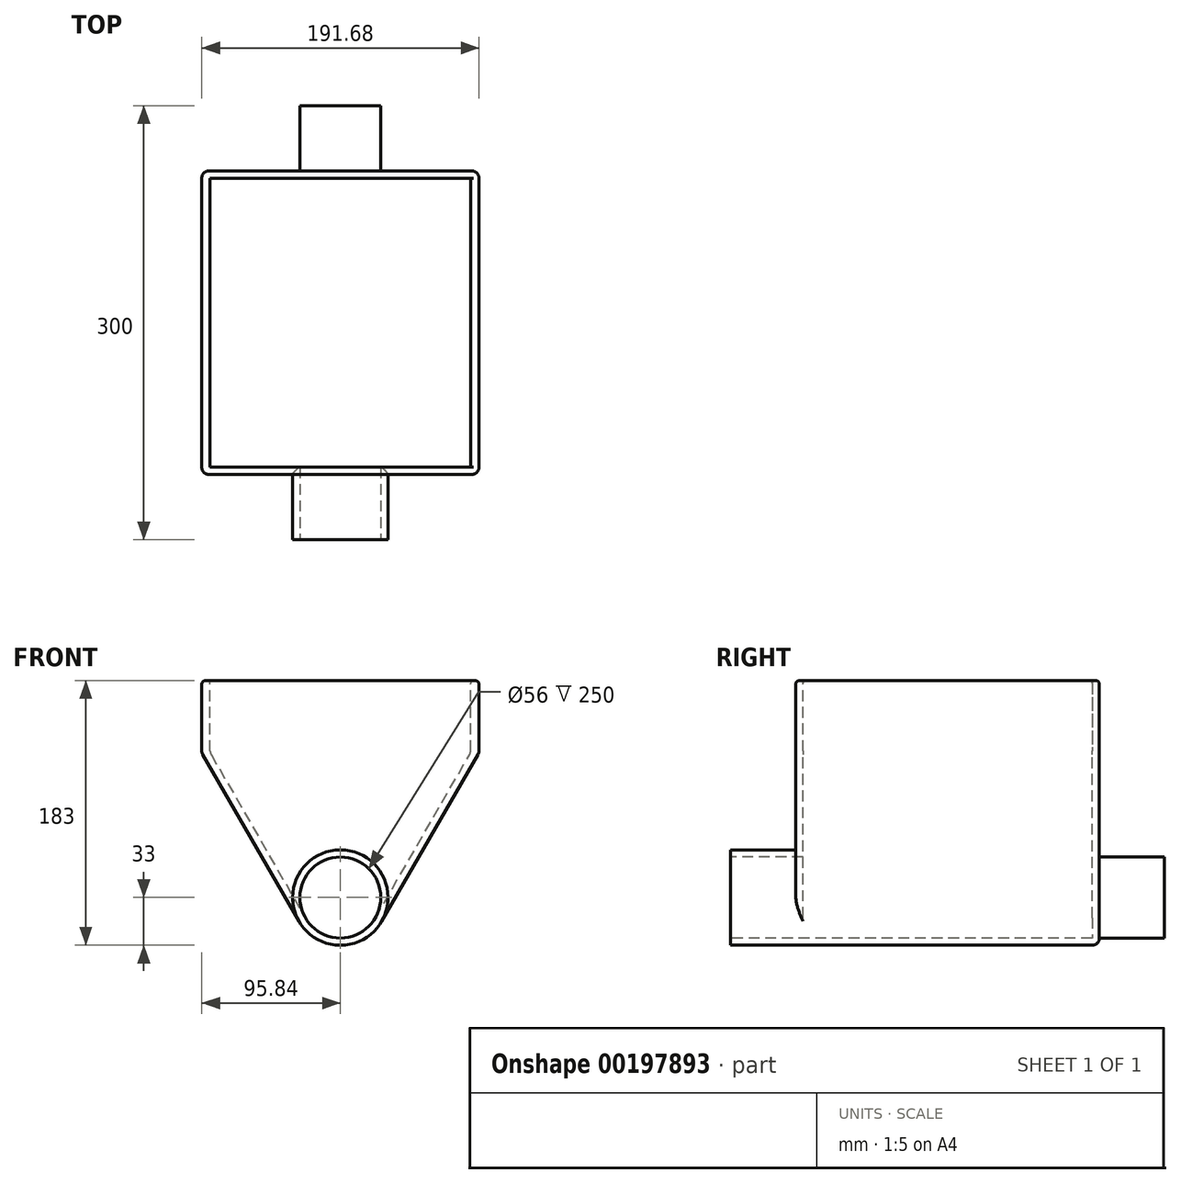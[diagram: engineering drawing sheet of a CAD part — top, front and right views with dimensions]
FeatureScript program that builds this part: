
annotation { "Feature Type Name" : "Feature", "Feature Type Description" : "" }
export const myFeature = defineFeature(function(context is Context, id is Id, definition is map)
    precondition{}
    {
        {
            var Q0;
            Q0=qCreatedBy(makeId("Front.planeOp"),FACE);
            var sketch = newSketch(context, id + "F0", { "sketchPlane" : qUnion([Q0])});
            skArc(sketch, "E0", {"start": v(-24.25, -14) * mm, "mid": v(0, -28) * mm, "end": v(24.25, -14) * mm});
            skArc(sketch, "E1", {"start": v(-28.58, -16.5) * mm, "mid": v(0, -33) * mm, "end": v(28.58, -16.5) * mm});
            skLineSegment(sketch, "E2", {"start": v(-28.58, -16.5) * mm, "end": v(-95.84, 100) * mm});
            skLineSegment(sketch, "E3", {"start": v(-95.84, 100) * mm, "end": v(-90.07, 100) * mm});
            skLineSegment(sketch, "E4", {"start": v(-90.07, 100) * mm, "end": v(-24.25, -14) * mm});
            skLineSegment(sketch, "E5", {"start": v(24.25, -14) * mm, "end": v(90.07, 100) * mm});
            skLineSegment(sketch, "E6", {"start": v(90.07, 100) * mm, "end": v(95.84, 100) * mm});
            skLineSegment(sketch, "E7", {"start": v(95.84, 100) * mm, "end": v(28.58, -16.5) * mm});
            skLineSegment(sketch, "E8", {"start": v(-95.84, 100) * mm, "end": v(-95.84, 150) * mm});
            skLineSegment(sketch, "E9", {"start": v(-95.84, 150) * mm, "end": v(-90.07, 150) * mm});
            skLineSegment(sketch, "E10", {"start": v(-90.07, 150) * mm, "end": v(-90.07, 100) * mm});
            skLineSegment(sketch, "E11", {"start": v(95.84, 100) * mm, "end": v(95.84, 150) * mm});
            skLineSegment(sketch, "E12", {"start": v(95.84, 150) * mm, "end": v(90.07, 150) * mm});
            skLineSegment(sketch, "E13", {"start": v(90.07, 150) * mm, "end": v(90.07, 100) * mm});
            skSolve(sketch);
        }
        {
            var Q0;
            Q0 = qSketchRegion(id + "F0", true);
            extrude(context, id + "F1", {"entities" : qUnion([Q0]), "oppositeDirection" : true, "depth" : 200 * mm});
        }
        {
            var Q0;
            Q0=makeQuery(id+"F1.opExtrude","CAP_FACE",FACE,{"disambiguationData":[OSD([sQuery(id+"F0.wireOp",EDGE,"E0"),sQuery(id+"F0.wireOp",EDGE,"E1"),sQuery(id+"F0.wireOp",EDGE,"E2"),sQuery(id+"F0.wireOp",EDGE,"E4"),sQuery(id+"F0.wireOp",EDGE,"E5"),sQuery(id+"F0.wireOp",EDGE,"E7"),sQuery(id+"F0.wireOp",EDGE,"E8"),sQuery(id+"F0.wireOp",EDGE,"E9"),sQuery(id+"F0.wireOp",EDGE,"E10"),sQuery(id+"F0.wireOp",EDGE,"E11"),sQuery(id+"F0.wireOp",EDGE,"E12"),sQuery(id+"F0.wireOp",EDGE,"E13")])],"isStart":true});
            var sketch = newSketch(context, id + "F2", { "sketchPlane" : qUnion([Q0])});
            skCircle(sketch, "E14", {"center": v(0, 0) * mm, "radius": 33 * mm});
            skCircle(sketch, "E15", {"center": v(0, 0) * mm, "radius": 28 * mm});
            skSolve(sketch);
        }
        {
            var Q0;
            {var subQ0=sQuery(id+"F2.wireOp",EDGE,"E14");var subQ1=makeQuery(id+"F1.opExtrude","CAP_EDGE",EDGE,{"disambiguationData":[OSD([sQuery(id+"F0.wireOp",EDGE,"E4")])],"isStart":true});var subQ2=makeQuery(id+"F2.imprint","INTERSECT",VERTEX,{"derivedFrom":[subQ1,subQ0]});Q0=makeQuery(id+"F2.imprint","IMPRINT",FACE,{"disambiguationData":[TD([[makeQuery(id+"F2.imprint","IMPRINT",EDGE,{"disambiguationData":[TD([[subQ2,1.0]])],"derivedFrom":subQ0}),1.0]])]});}
            var Q1;
            {var subQ5=sQuery(id+"F2.wireOp",EDGE,"E14");var subQ8=makeQuery(id+"F2.imprint","INTERSECT",VERTEX,{"derivedFrom":[makeQuery(id+"F1.opExtrude","CAP_EDGE",EDGE,{"disambiguationData":[OSD([sQuery(id+"F0.wireOp",EDGE,"E2")])],"isStart":true}),subQ5]});Q1=makeQuery(id+"F2.imprint","IMPRINT",FACE,{"disambiguationData":[TD([[makeQuery(id+"F2.imprint","IMPRINT",EDGE,{"disambiguationData":[TD([[subQ8,-1.0]])],"derivedFrom":subQ5}),1.0]])]});}
            extrude(context, id + "F3", {"entities" : qUnion([Q0, Q1]), "operationType" : NewBodyOperationType.ADD, "depth" : 50 * mm});
        }
        {
            var Q0;
            Q0=makeQuery(id+"F1.opExtrude","CAP_FACE",FACE,{"disambiguationData":[OSD([sQuery(id+"F0.wireOp",EDGE,"E0"),sQuery(id+"F0.wireOp",EDGE,"E1"),sQuery(id+"F0.wireOp",EDGE,"E2"),sQuery(id+"F0.wireOp",EDGE,"E4"),sQuery(id+"F0.wireOp",EDGE,"E5"),sQuery(id+"F0.wireOp",EDGE,"E7"),sQuery(id+"F0.wireOp",EDGE,"E8"),sQuery(id+"F0.wireOp",EDGE,"E9"),sQuery(id+"F0.wireOp",EDGE,"E10"),sQuery(id+"F0.wireOp",EDGE,"E11"),sQuery(id+"F0.wireOp",EDGE,"E12"),sQuery(id+"F0.wireOp",EDGE,"E13")])],"isStart":false});
            var sketch = newSketch(context, id + "F4", { "sketchPlane" : qUnion([Q0])});
            skCircle(sketch, "E16", {"center": v(0, 0) * mm, "radius": 28 * mm});
            skCircle(sketch, "E17", {"center": v(0, 0) * mm, "radius": 33 * mm});
            skSolve(sketch);
        }
        {
            var Q0;
            {var subQ0=sQuery(id+"F4.wireOp",EDGE,"E16");Q0=makeQuery(id+"F4.imprint","IMPRINT",FACE,{"disambiguationData":[TD([[makeQuery(id+"F4.imprint","IMPRINT",EDGE,{"disambiguationData":[OD(1.0)],"derivedFrom":subQ0}),-1.0]])]});}
            var Q1;
            {var subQ7=sQuery(id+"F4.wireOp",EDGE,"E16");Q1=makeQuery(id+"F4.imprint","IMPRINT",FACE,{"disambiguationData":[TD([[makeQuery(id+"F4.imprint","IMPRINT",EDGE,{"disambiguationData":[OD(0.0)],"derivedFrom":subQ7}),1.0]])]});}
            extrude(context, id + "F5", {"entities" : qUnion([Q0, Q1]), "operationType" : NewBodyOperationType.ADD, "depth" : 50 * mm});
        }
        {
            var Q0;
            {var subQ0=sQuery(id+"F0.wireOp",EDGE,"E11");var subQ1=sQuery(id+"F0.wireOp",EDGE,"E7");var subQ2=sQuery(id+"F0.wireOp",EDGE,"E5");var subQ3=sQuery(id+"F0.wireOp",EDGE,"E1");var subQ4=sQuery(id+"F0.wireOp",EDGE,"E12");var subQ6=sQuery(id+"F0.wireOp",EDGE,"E13");Q0=makeQuery(id+"F3.boolean.opBoolean","SPLIT",FACE,{"disambiguationData":[TD([makeQuery(id+"F1.opExtrude","SWEPT_FACE",FACE,{"disambiguationData":[OSD([subQ2])]})])],"derivedFrom":makeQuery(id+"F1.opExtrude","CAP_FACE",FACE,{"disambiguationData":[OSD([sQuery(id+"F0.wireOp",EDGE,"E0"),subQ3,sQuery(id+"F0.wireOp",EDGE,"E2"),sQuery(id+"F0.wireOp",EDGE,"E4"),subQ2,subQ1,sQuery(id+"F0.wireOp",EDGE,"E8"),sQuery(id+"F0.wireOp",EDGE,"E9"),sQuery(id+"F0.wireOp",EDGE,"E10"),subQ0,subQ4,subQ6])],"isStart":true})});}
            var Q1;
            {var subQ0=sQuery(id+"F0.wireOp",EDGE,"E4");var subQ2=sQuery(id+"F0.wireOp",EDGE,"E2");var subQ3=sQuery(id+"F0.wireOp",EDGE,"E8");var subQ4=sQuery(id+"F0.wireOp",EDGE,"E1");var subQ5=sQuery(id+"F0.wireOp",EDGE,"E10");var subQ6=sQuery(id+"F0.wireOp",EDGE,"E9");Q1=makeQuery(id+"F3.boolean.opBoolean","SPLIT",FACE,{"disambiguationData":[TD([makeQuery(id+"F1.opExtrude","SWEPT_FACE",FACE,{"disambiguationData":[OSD([subQ2])]})])],"derivedFrom":makeQuery(id+"F1.opExtrude","CAP_FACE",FACE,{"disambiguationData":[OSD([sQuery(id+"F0.wireOp",EDGE,"E0"),subQ4,subQ2,subQ0,sQuery(id+"F0.wireOp",EDGE,"E5"),sQuery(id+"F0.wireOp",EDGE,"E7"),subQ3,subQ6,subQ5,sQuery(id+"F0.wireOp",EDGE,"E11"),sQuery(id+"F0.wireOp",EDGE,"E12"),sQuery(id+"F0.wireOp",EDGE,"E13")])],"isStart":true})});}
            extrude(context, id + "F6", {"entities" : qUnion([Q0, Q1]), "operationType" : NewBodyOperationType.ADD, "depth" : 5 * mm});
        }
        {
            var Q0;
            Q0=qCreatedBy(makeId("Right.planeOp"),FACE);
            var sketch = newSketch(context, id + "F7", { "sketchPlane" : qUnion([Q0])});
            skLineSegment(sketch, "E18.bottom", {"start": v(-5, 110) * mm, "end": v(0, 110) * mm});
            skLineSegment(sketch, "E18.top", {"start": v(-5, 150) * mm, "end": v(0, 150) * mm});
            skLineSegment(sketch, "E18.left", {"start": v(-5, 110) * mm, "end": v(-5, 150) * mm});
            skLineSegment(sketch, "E18.right", {"start": v(0, 110) * mm, "end": v(0, 150) * mm});
            skSolve(sketch);
        }
        {
            var Q0;
            Q0=makeQuery(id+"F7.imprint","IMPRINT",FACE,{"disambiguationData":[TD([[makeQuery(id+"F7.imprint","IMPRINT",EDGE,{"derivedFrom":sQuery(id+"F7.wireOp",EDGE,"E18.bottom")}),1.0]])]});
            var Q1;
            {var subQ0=sQuery(id+"F0.wireOp",EDGE,"E10");Q1=makeQuery(id+"F6.boolean.opBoolean","MERGE",FACE,{"derivedFrom":[makeQuery(id+"F1.opExtrude","SWEPT_FACE",FACE,{"disambiguationData":[OSD([subQ0])]}),makeQuery(id+"F6.opExtrude","SWEPT_FACE",FACE,{"disambiguationData":[OSD([subQ0])]})]});}
            var Q2;
            {var subQ0=sQuery(id+"F0.wireOp",EDGE,"E13");Q2=makeQuery(id+"F6.boolean.opBoolean","MERGE",FACE,{"derivedFrom":[makeQuery(id+"F1.opExtrude","SWEPT_FACE",FACE,{"disambiguationData":[OSD([subQ0])]}),makeQuery(id+"F6.opExtrude","SWEPT_FACE",FACE,{"disambiguationData":[OSD([subQ0])]})]});}
            extrude(context, id + "F8", {"entities" : qUnion([Q0]), "endBound" : BoundingType.UP_TO_SURFACE, "oppositeDirection" : true, "endBoundEntityFace" : qUnion([Q1]), "depth" : 25 * mm, "hasSecondDirection" : true, "secondDirectionBound" : SecondDirectionBoundingType.UP_TO_SURFACE, "secondDirectionOppositeDirection" : false, "secondDirectionBoundEntityFace" : qUnion([Q2]), "secondDirectionDepth" : 25 * mm});
        }
        {
            var Q0;
            Q0=makeQuery(id+"F8.opExtrude","SWEPT_FACE",FACE,{"disambiguationData":[OSD([sQuery(id+"F7.wireOp",EDGE,"E18.bottom")])]});
            var Q1;
            Q1=makeQuery(id+"F1.opExtrude","SWEPT_BODY",BODY,{"disambiguationData":[OSD([sQuery(id+"F0.wireOp",EDGE,"E0"),sQuery(id+"F0.wireOp",EDGE,"E1"),sQuery(id+"F0.wireOp",EDGE,"E2"),sQuery(id+"F0.wireOp",EDGE,"E4"),sQuery(id+"F0.wireOp",EDGE,"E5"),sQuery(id+"F0.wireOp",EDGE,"E7"),sQuery(id+"F0.wireOp",EDGE,"E8"),sQuery(id+"F0.wireOp",EDGE,"E9"),sQuery(id+"F0.wireOp",EDGE,"E10"),sQuery(id+"F0.wireOp",EDGE,"E11"),sQuery(id+"F0.wireOp",EDGE,"E12"),sQuery(id+"F0.wireOp",EDGE,"E13")])]});
            extrude(context, id + "F9", {"entities" : qUnion([Q0]), "operationType" : NewBodyOperationType.ADD, "endBound" : BoundingType.UP_TO_BODY, "endBoundEntityBody" : qUnion([Q1]), "depth" : 25 * mm});
        }
        {
            var Q0;
            {var subQ0=sQuery(id+"F0.wireOp",EDGE,"E11");var subQ1=sQuery(id+"F0.wireOp",EDGE,"E7");var subQ2=sQuery(id+"F0.wireOp",EDGE,"E5");var subQ3=sQuery(id+"F0.wireOp",EDGE,"E1");var subQ4=sQuery(id+"F0.wireOp",EDGE,"E12");var subQ5=sQuery(id+"F0.wireOp",EDGE,"E13");Q0=makeQuery(id+"F5.boolean.opBoolean","SPLIT",FACE,{"disambiguationData":[TD([makeQuery(id+"F1.opExtrude","SWEPT_FACE",FACE,{"disambiguationData":[OSD([subQ2])]})])],"derivedFrom":makeQuery(id+"F1.opExtrude","CAP_FACE",FACE,{"disambiguationData":[OSD([sQuery(id+"F0.wireOp",EDGE,"E0"),subQ3,sQuery(id+"F0.wireOp",EDGE,"E2"),sQuery(id+"F0.wireOp",EDGE,"E4"),subQ2,subQ1,sQuery(id+"F0.wireOp",EDGE,"E8"),sQuery(id+"F0.wireOp",EDGE,"E9"),sQuery(id+"F0.wireOp",EDGE,"E10"),subQ0,subQ4,subQ5])],"isStart":false})});}
            var Q1;
            {var subQ0=sQuery(id+"F0.wireOp",EDGE,"E4");var subQ1=sQuery(id+"F0.wireOp",EDGE,"E2");var subQ2=sQuery(id+"F0.wireOp",EDGE,"E8");var subQ3=sQuery(id+"F0.wireOp",EDGE,"E1");var subQ4=sQuery(id+"F0.wireOp",EDGE,"E10");var subQ5=sQuery(id+"F0.wireOp",EDGE,"E9");Q1=makeQuery(id+"F5.boolean.opBoolean","SPLIT",FACE,{"disambiguationData":[TD([makeQuery(id+"F1.opExtrude","SWEPT_FACE",FACE,{"disambiguationData":[OSD([subQ1])]})])],"derivedFrom":makeQuery(id+"F1.opExtrude","CAP_FACE",FACE,{"disambiguationData":[OSD([sQuery(id+"F0.wireOp",EDGE,"E0"),subQ3,subQ1,subQ0,sQuery(id+"F0.wireOp",EDGE,"E5"),sQuery(id+"F0.wireOp",EDGE,"E7"),subQ2,subQ5,subQ4,sQuery(id+"F0.wireOp",EDGE,"E11"),sQuery(id+"F0.wireOp",EDGE,"E12"),sQuery(id+"F0.wireOp",EDGE,"E13")])],"isStart":false})});}
            extrude(context, id + "F10", {"entities" : qUnion([Q0, Q1]), "operationType" : NewBodyOperationType.ADD, "depth" : 5 * mm});
        }
        {
            var Q0;
            Q0=qCreatedBy(makeId("Right.planeOp"),FACE);
            var sketch = newSketch(context, id + "F11", { "sketchPlane" : qUnion([Q0])});
            skLineSegment(sketch, "E19.bottom", {"start": v(205, 150) * mm, "end": v(200, 150) * mm});
            skLineSegment(sketch, "E19.top", {"start": v(205, 110) * mm, "end": v(200, 110) * mm});
            skLineSegment(sketch, "E19.left", {"start": v(205, 150) * mm, "end": v(205, 110) * mm});
            skLineSegment(sketch, "E19.right", {"start": v(200, 150) * mm, "end": v(200, 110) * mm});
            skSolve(sketch);
        }
        {
            var Q0;
            Q0 = qSketchRegion(id + "F11", true);
            var Q1;
            {var subQ0=sQuery(id+"F0.wireOp",EDGE,"E10");Q1=makeQuery(id+"F10.boolean.opBoolean","MERGE",FACE,{"derivedFrom":[makeQuery(id+"F6.boolean.opBoolean","MERGE",FACE,{"derivedFrom":[makeQuery(id+"F1.opExtrude","SWEPT_FACE",FACE,{"disambiguationData":[OSD([subQ0])]}),makeQuery(id+"F6.opExtrude","SWEPT_FACE",FACE,{"disambiguationData":[OSD([subQ0])]})]}),makeQuery(id+"F10.opExtrude","SWEPT_FACE",FACE,{"disambiguationData":[OSD([subQ0])]})]});}
            var Q2;
            {var subQ0=sQuery(id+"F0.wireOp",EDGE,"E13");Q2=makeQuery(id+"F10.boolean.opBoolean","MERGE",FACE,{"derivedFrom":[makeQuery(id+"F6.boolean.opBoolean","MERGE",FACE,{"derivedFrom":[makeQuery(id+"F1.opExtrude","SWEPT_FACE",FACE,{"disambiguationData":[OSD([subQ0])]}),makeQuery(id+"F6.opExtrude","SWEPT_FACE",FACE,{"disambiguationData":[OSD([subQ0])]})]}),makeQuery(id+"F10.opExtrude","SWEPT_FACE",FACE,{"disambiguationData":[OSD([subQ0])]})]});}
            extrude(context, id + "F12", {"entities" : qUnion([Q0]), "endBound" : BoundingType.UP_TO_SURFACE, "oppositeDirection" : true, "endBoundEntityFace" : qUnion([Q1]), "depth" : 25 * mm, "hasSecondDirection" : true, "secondDirectionBound" : SecondDirectionBoundingType.UP_TO_SURFACE, "secondDirectionOppositeDirection" : false, "secondDirectionBoundEntityFace" : qUnion([Q2]), "secondDirectionDepth" : 25 * mm});
        }
        {
            var Q0;
            Q0=makeQuery(id+"F12.opExtrude","SWEPT_FACE",FACE,{"disambiguationData":[OSD([sQuery(id+"F11.wireOp",EDGE,"E19.top")])]});
            var Q1;
            Q1=makeQuery(id+"F1.opExtrude","SWEPT_BODY",BODY,{"disambiguationData":[OSD([sQuery(id+"F0.wireOp",EDGE,"E0"),sQuery(id+"F0.wireOp",EDGE,"E1"),sQuery(id+"F0.wireOp",EDGE,"E2"),sQuery(id+"F0.wireOp",EDGE,"E4"),sQuery(id+"F0.wireOp",EDGE,"E5"),sQuery(id+"F0.wireOp",EDGE,"E7"),sQuery(id+"F0.wireOp",EDGE,"E8"),sQuery(id+"F0.wireOp",EDGE,"E9"),sQuery(id+"F0.wireOp",EDGE,"E10"),sQuery(id+"F0.wireOp",EDGE,"E11"),sQuery(id+"F0.wireOp",EDGE,"E12"),sQuery(id+"F0.wireOp",EDGE,"E13")])]});
            extrude(context, id + "F13", {"entities" : qUnion([Q0]), "operationType" : NewBodyOperationType.ADD, "endBound" : BoundingType.UP_TO_BODY, "endBoundEntityBody" : qUnion([Q1]), "depth" : 25 * mm});
        }
        {
            var Q0;
            {var subQ0=sQuery(id+"F0.wireOp",EDGE,"E5");var subQ1=makeQuery(id+"F1.opExtrude","SWEPT_FACE",FACE,{"disambiguationData":[OSD([subQ0])]});var subQ3=sQuery(id+"F0.wireOp",EDGE,"E0");Q0=makeQuery(id+"F9.boolean.opBoolean","MERGE",EDGE,{"derivedFrom":[makeQuery(id+"F3.boolean.opBoolean","SPLIT",EDGE,{"disambiguationData":[TD([makeQuery(id+"F1.opExtrude","SWEPT_FACE",FACE,{"disambiguationData":[OSD([subQ3])]})])],"derivedFrom":makeQuery(id+"F1.opExtrude","CAP_EDGE",EDGE,{"disambiguationData":[OSD([subQ0])],"isStart":true})}),makeQuery(id+"F9.opExtrude","TWEAK_EDGE",EDGE,{"derivedFrom":[makeQuery(id+"F6.boolean.opBoolean","MERGE",FACE,{"derivedFrom":[subQ1,makeQuery(id+"F6.opExtrude","SWEPT_FACE",FACE,{"disambiguationData":[OSD([subQ0])]})]}),makeQuery(id+"F8.opExtrude","TWEAK_EDGE",EDGE,{"derivedFrom":[makeQuery(id+"F7.imprint","IMPRINT",EDGE,{"derivedFrom":sQuery(id+"F7.wireOp",EDGE,"E18.bottom")}),makeQuery(id+"F7.imprint","IMPRINT",EDGE,{"derivedFrom":sQuery(id+"F7.wireOp",EDGE,"E18.right")})]})]})]});}
            var Q1;
            {var subQ0=sQuery(id+"F7.wireOp",EDGE,"E18.right");var subQ1=sQuery(id+"F0.wireOp",EDGE,"E13");Q1=makeQuery(id+"F9.boolean.opBoolean","MERGE",EDGE,{"derivedFrom":[makeQuery(id+"F8.opExtrude","TWEAK_EDGE",EDGE,{"derivedFrom":[makeQuery(id+"F6.boolean.opBoolean","MERGE",FACE,{"derivedFrom":[makeQuery(id+"F1.opExtrude","SWEPT_FACE",FACE,{"disambiguationData":[OSD([subQ1])]}),makeQuery(id+"F6.opExtrude","SWEPT_FACE",FACE,{"disambiguationData":[OSD([subQ1])]})]}),makeQuery(id+"F7.imprint","IMPRINT",EDGE,{"derivedFrom":subQ0})]}),makeQuery(id+"F9.opExtrude","SWEPT_EDGE",EDGE,{"disambiguationData":[OSD([subQ1,sQuery(id+"F7.wireOp",EDGE,"E18.bottom"),subQ0])]})]});}
            var Q2;
            {var subQ0=sQuery(id+"F0.wireOp",EDGE,"E4");var subQ1=makeQuery(id+"F1.opExtrude","SWEPT_FACE",FACE,{"disambiguationData":[OSD([subQ0])]});var subQ4=sQuery(id+"F0.wireOp",EDGE,"E0");Q2=makeQuery(id+"F9.boolean.opBoolean","MERGE",EDGE,{"derivedFrom":[makeQuery(id+"F3.boolean.opBoolean","SPLIT",EDGE,{"disambiguationData":[TD([makeQuery(id+"F1.opExtrude","SWEPT_FACE",FACE,{"disambiguationData":[OSD([subQ4])]})])],"derivedFrom":makeQuery(id+"F1.opExtrude","CAP_EDGE",EDGE,{"disambiguationData":[OSD([subQ0])],"isStart":true})}),makeQuery(id+"F9.opExtrude","TWEAK_EDGE",EDGE,{"derivedFrom":[makeQuery(id+"F6.boolean.opBoolean","MERGE",FACE,{"derivedFrom":[subQ1,makeQuery(id+"F6.opExtrude","SWEPT_FACE",FACE,{"disambiguationData":[OSD([subQ0])]})]}),makeQuery(id+"F8.opExtrude","TWEAK_EDGE",EDGE,{"derivedFrom":[makeQuery(id+"F7.imprint","IMPRINT",EDGE,{"derivedFrom":sQuery(id+"F7.wireOp",EDGE,"E18.bottom")}),makeQuery(id+"F7.imprint","IMPRINT",EDGE,{"derivedFrom":sQuery(id+"F7.wireOp",EDGE,"E18.right")})]})]})]});}
            var Q3;
            {var subQ0=sQuery(id+"F7.wireOp",EDGE,"E18.right");var subQ1=sQuery(id+"F0.wireOp",EDGE,"E10");Q3=makeQuery(id+"F9.boolean.opBoolean","MERGE",EDGE,{"derivedFrom":[makeQuery(id+"F8.opExtrude","TWEAK_EDGE",EDGE,{"derivedFrom":[makeQuery(id+"F6.boolean.opBoolean","MERGE",FACE,{"derivedFrom":[makeQuery(id+"F1.opExtrude","SWEPT_FACE",FACE,{"disambiguationData":[OSD([subQ1])]}),makeQuery(id+"F6.opExtrude","SWEPT_FACE",FACE,{"disambiguationData":[OSD([subQ1])]})]}),makeQuery(id+"F7.imprint","IMPRINT",EDGE,{"derivedFrom":subQ0})]}),makeQuery(id+"F9.opExtrude","SWEPT_EDGE",EDGE,{"disambiguationData":[OSD([subQ1,sQuery(id+"F7.wireOp",EDGE,"E18.bottom"),subQ0])]})]});}
            var Q4;
            {var subQ0=sQuery(id+"F11.wireOp",EDGE,"E19.right");var subQ1=sQuery(id+"F0.wireOp",EDGE,"E10");Q4=makeQuery(id+"F13.boolean.opBoolean","MERGE",EDGE,{"derivedFrom":[makeQuery(id+"F12.opExtrude","TWEAK_EDGE",EDGE,{"derivedFrom":[makeQuery(id+"F10.boolean.opBoolean","MERGE",FACE,{"derivedFrom":[makeQuery(id+"F6.boolean.opBoolean","MERGE",FACE,{"derivedFrom":[makeQuery(id+"F1.opExtrude","SWEPT_FACE",FACE,{"disambiguationData":[OSD([subQ1])]}),makeQuery(id+"F6.opExtrude","SWEPT_FACE",FACE,{"disambiguationData":[OSD([subQ1])]})]}),makeQuery(id+"F10.opExtrude","SWEPT_FACE",FACE,{"disambiguationData":[OSD([subQ1])]})]}),makeQuery(id+"F11.imprint","IMPRINT",EDGE,{"derivedFrom":subQ0})]}),makeQuery(id+"F13.opExtrude","SWEPT_EDGE",EDGE,{"disambiguationData":[OSD([subQ1,sQuery(id+"F11.wireOp",EDGE,"E19.top"),subQ0])]})]});}
            var Q5;
            {var subQ0=sQuery(id+"F0.wireOp",EDGE,"E4");var subQ1=makeQuery(id+"F1.opExtrude","SWEPT_FACE",FACE,{"disambiguationData":[OSD([subQ0])]});var subQ3=sQuery(id+"F0.wireOp",EDGE,"E0");Q5=makeQuery(id+"F13.boolean.opBoolean","MERGE",EDGE,{"derivedFrom":[makeQuery(id+"F5.boolean.opBoolean","SPLIT",EDGE,{"disambiguationData":[TD([makeQuery(id+"F1.opExtrude","SWEPT_FACE",FACE,{"disambiguationData":[OSD([subQ3])]})])],"derivedFrom":makeQuery(id+"F1.opExtrude","CAP_EDGE",EDGE,{"disambiguationData":[OSD([subQ0])],"isStart":false})}),makeQuery(id+"F13.opExtrude","TWEAK_EDGE",EDGE,{"derivedFrom":[makeQuery(id+"F10.boolean.opBoolean","MERGE",FACE,{"derivedFrom":[makeQuery(id+"F6.boolean.opBoolean","MERGE",FACE,{"derivedFrom":[subQ1,makeQuery(id+"F6.opExtrude","SWEPT_FACE",FACE,{"disambiguationData":[OSD([subQ0])]})]}),makeQuery(id+"F10.opExtrude","SWEPT_FACE",FACE,{"disambiguationData":[OSD([subQ0])]})]}),makeQuery(id+"F12.opExtrude","TWEAK_EDGE",EDGE,{"derivedFrom":[makeQuery(id+"F11.imprint","IMPRINT",EDGE,{"derivedFrom":sQuery(id+"F11.wireOp",EDGE,"E19.top")}),makeQuery(id+"F11.imprint","IMPRINT",EDGE,{"derivedFrom":sQuery(id+"F11.wireOp",EDGE,"E19.right")})]})]})]});}
            var Q6;
            {var subQ0=sQuery(id+"F11.wireOp",EDGE,"E19.right");var subQ1=sQuery(id+"F0.wireOp",EDGE,"E13");Q6=makeQuery(id+"F13.boolean.opBoolean","MERGE",EDGE,{"derivedFrom":[makeQuery(id+"F12.opExtrude","TWEAK_EDGE",EDGE,{"derivedFrom":[makeQuery(id+"F10.boolean.opBoolean","MERGE",FACE,{"derivedFrom":[makeQuery(id+"F6.boolean.opBoolean","MERGE",FACE,{"derivedFrom":[makeQuery(id+"F1.opExtrude","SWEPT_FACE",FACE,{"disambiguationData":[OSD([subQ1])]}),makeQuery(id+"F6.opExtrude","SWEPT_FACE",FACE,{"disambiguationData":[OSD([subQ1])]})]}),makeQuery(id+"F10.opExtrude","SWEPT_FACE",FACE,{"disambiguationData":[OSD([subQ1])]})]}),makeQuery(id+"F11.imprint","IMPRINT",EDGE,{"derivedFrom":subQ0})]}),makeQuery(id+"F13.opExtrude","SWEPT_EDGE",EDGE,{"disambiguationData":[OSD([subQ1,sQuery(id+"F11.wireOp",EDGE,"E19.top"),subQ0])]})]});}
            var Q7;
            {var subQ0=sQuery(id+"F0.wireOp",EDGE,"E5");var subQ1=makeQuery(id+"F1.opExtrude","SWEPT_FACE",FACE,{"disambiguationData":[OSD([subQ0])]});var subQ4=sQuery(id+"F0.wireOp",EDGE,"E0");Q7=makeQuery(id+"F13.boolean.opBoolean","MERGE",EDGE,{"derivedFrom":[makeQuery(id+"F5.boolean.opBoolean","SPLIT",EDGE,{"disambiguationData":[TD([makeQuery(id+"F1.opExtrude","SWEPT_FACE",FACE,{"disambiguationData":[OSD([subQ4])]})])],"derivedFrom":makeQuery(id+"F1.opExtrude","CAP_EDGE",EDGE,{"disambiguationData":[OSD([subQ0])],"isStart":false})}),makeQuery(id+"F13.opExtrude","TWEAK_EDGE",EDGE,{"derivedFrom":[makeQuery(id+"F10.boolean.opBoolean","MERGE",FACE,{"derivedFrom":[makeQuery(id+"F6.boolean.opBoolean","MERGE",FACE,{"derivedFrom":[subQ1,makeQuery(id+"F6.opExtrude","SWEPT_FACE",FACE,{"disambiguationData":[OSD([subQ0])]})]}),makeQuery(id+"F10.opExtrude","SWEPT_FACE",FACE,{"disambiguationData":[OSD([subQ0])]})]}),makeQuery(id+"F12.opExtrude","TWEAK_EDGE",EDGE,{"derivedFrom":[makeQuery(id+"F11.imprint","IMPRINT",EDGE,{"derivedFrom":sQuery(id+"F11.wireOp",EDGE,"E19.top")}),makeQuery(id+"F11.imprint","IMPRINT",EDGE,{"derivedFrom":sQuery(id+"F11.wireOp",EDGE,"E19.right")})]})]})]});}
            var Q8;
            {var subQ0=sQuery(id+"F0.wireOp",EDGE,"E13");var subQ1=sQuery(id+"F0.wireOp",EDGE,"E6");var subQ2=sQuery(id+"F0.wireOp",EDGE,"E5");Q8=makeQuery(id+"F10.boolean.opBoolean","MERGE",EDGE,{"derivedFrom":[makeQuery(id+"F6.boolean.opBoolean","MERGE",EDGE,{"derivedFrom":[makeQuery(id+"F1.opExtrude","SWEPT_EDGE",EDGE,{"disambiguationData":[OSD([subQ2,subQ1,subQ0])]}),makeQuery(id+"F6.opExtrude","SWEPT_EDGE",EDGE,{"disambiguationData":[OSD([subQ2,subQ1,subQ0])]})]}),makeQuery(id+"F10.opExtrude","SWEPT_EDGE",EDGE,{"disambiguationData":[OSD([subQ2,subQ1,subQ0])]})]});}
            var Q9;
            {var subQ0=sQuery(id+"F0.wireOp",EDGE,"E10");var subQ1=sQuery(id+"F0.wireOp",EDGE,"E4");var subQ2=sQuery(id+"F0.wireOp",EDGE,"E3");Q9=makeQuery(id+"F10.boolean.opBoolean","MERGE",EDGE,{"derivedFrom":[makeQuery(id+"F6.boolean.opBoolean","MERGE",EDGE,{"derivedFrom":[makeQuery(id+"F1.opExtrude","SWEPT_EDGE",EDGE,{"disambiguationData":[OSD([subQ2,subQ1,subQ0])]}),makeQuery(id+"F6.opExtrude","SWEPT_EDGE",EDGE,{"disambiguationData":[OSD([subQ2,subQ1,subQ0])]})]}),makeQuery(id+"F10.opExtrude","SWEPT_EDGE",EDGE,{"disambiguationData":[OSD([subQ2,subQ1,subQ0])]})]});}
            fillet(context, id + "F14", {"entities" : qUnion([Q0, Q1, Q2, Q3, Q4, Q5, Q6, Q7, Q8, Q9]), "radius" : 5 * mm, "tangentPropagation" : true, "allowEdgeOverflow" : false});
        }
        {
            var Q0;
            {var subQ0=sQuery(id+"F0.wireOp",EDGE,"E13");var subQ1=sQuery(id+"F0.wireOp",EDGE,"E12");Q0=makeQuery(id+"F10.boolean.opBoolean","MERGE",EDGE,{"derivedFrom":[makeQuery(id+"F6.boolean.opBoolean","MERGE",EDGE,{"derivedFrom":[makeQuery(id+"F1.opExtrude","SWEPT_EDGE",EDGE,{"disambiguationData":[OSD([subQ1,subQ0])]}),makeQuery(id+"F6.opExtrude","SWEPT_EDGE",EDGE,{"disambiguationData":[OSD([subQ1,subQ0])]})]}),makeQuery(id+"F10.opExtrude","SWEPT_EDGE",EDGE,{"disambiguationData":[OSD([subQ1,subQ0])]})]});}
            fillet(context, id + "F15", {"entities" : qUnion([Q0]), "radius" : 2 * mm, "tangentPropagation" : true, "allowEdgeOverflow" : false});
        }
        {
            var Q0;
            Q0=makeQuery(id+"F6.opExtrude","CAP_EDGE",EDGE,{"disambiguationData":[OSD([sQuery(id+"F0.wireOp",EDGE,"E8")])],"isStart":false});
            var Q1;
            Q1=makeQuery(id+"F6.opExtrude","CAP_EDGE",EDGE,{"disambiguationData":[OSD([sQuery(id+"F0.wireOp",EDGE,"E2")])],"isStart":false});
            var Q2;
            {var subQ0=sQuery(id+"F2.wireOp",EDGE,"E14");var subQ1=makeQuery(id+"F3.opExtrude","SWEPT_FACE",FACE,{"disambiguationData":[OSD([subQ0])]});var subQ2=sQuery(id+"F0.wireOp",EDGE,"E1");var subQ3=makeQuery(id+"F1.opExtrude","SWEPT_FACE",FACE,{"disambiguationData":[OSD([subQ2])]});var subQ4=sQuery(id+"F0.wireOp",EDGE,"E7");var subQ5=sQuery(id+"F0.wireOp",EDGE,"E5");var subQ6=sQuery(id+"F0.wireOp",EDGE,"E4");var subQ7=sQuery(id+"F0.wireOp",EDGE,"E2");var subQ8=makeQuery(id+"F1.opExtrude","CAP_FACE",FACE,{"disambiguationData":[OSD([sQuery(id+"F0.wireOp",EDGE,"E0"),subQ2,subQ7,subQ6,subQ5,subQ4,sQuery(id+"F0.wireOp",EDGE,"E8"),sQuery(id+"F0.wireOp",EDGE,"E9"),sQuery(id+"F0.wireOp",EDGE,"E10"),sQuery(id+"F0.wireOp",EDGE,"E11"),sQuery(id+"F0.wireOp",EDGE,"E12"),sQuery(id+"F0.wireOp",EDGE,"E13")])],"isStart":true});var subQ9=makeQuery(id+"F3.opExtrude","CAP_FACE",FACE,{"disambiguationData":[OSD([subQ0,sQuery(id+"F2.wireOp",EDGE,"E15")])],"isStart":true});var subQ10=makeQuery(id+"F3.opExtrude","CAP_EDGE",EDGE,{"disambiguationData":[OSD([subQ0])],"isStart":true});Q2=makeQuery(id+"F9.boolean.opBoolean","MERGE",EDGE,{"derivedFrom":[makeQuery(id+"F6.opExtrude","CAP_EDGE",EDGE,{"disambiguationData":[OSD([subQ0]),TDD([makeQuery(id+"F3.boolean.opBoolean","SPLIT",EDGE,{"disambiguationData":[TD([subQ8,subQ3,makeQuery(id+"F1.opExtrude","SWEPT_FACE",FACE,{"disambiguationData":[OSD([subQ7])]}),makeQuery(id+"F1.opExtrude","SWEPT_FACE",FACE,{"disambiguationData":[OSD([subQ6])]}),subQ1,subQ9])],"derivedFrom":subQ10})])],"isStart":false}),makeQuery(id+"F6.opExtrude","CAP_EDGE",EDGE,{"disambiguationData":[OSD([subQ0]),TDD([makeQuery(id+"F3.boolean.opBoolean","SPLIT",EDGE,{"disambiguationData":[TD([subQ8,subQ3,makeQuery(id+"F1.opExtrude","SWEPT_FACE",FACE,{"disambiguationData":[OSD([subQ5])]}),makeQuery(id+"F1.opExtrude","SWEPT_FACE",FACE,{"disambiguationData":[OSD([subQ4])]}),subQ1,subQ9])],"derivedFrom":subQ10})])],"isStart":false}),makeQuery(id+"F9.opExtrude","TWEAK_EDGE",EDGE,{"derivedFrom":[makeQuery(id+"F5.boolean.opBoolean","MERGE",FACE,{"derivedFrom":[makeQuery(id+"F3.boolean.opBoolean","MERGE",FACE,{"derivedFrom":[subQ3,subQ1]}),makeQuery(id+"F5.opExtrude","SWEPT_FACE",FACE,{"disambiguationData":[OSD([sQuery(id+"F4.wireOp",EDGE,"E17")])]})]}),makeQuery(id+"F8.opExtrude","TWEAK_EDGE",EDGE,{"derivedFrom":[makeQuery(id+"F7.imprint","IMPRINT",EDGE,{"derivedFrom":sQuery(id+"F7.wireOp",EDGE,"E18.bottom")}),makeQuery(id+"F7.imprint","IMPRINT",EDGE,{"derivedFrom":sQuery(id+"F7.wireOp",EDGE,"E18.left")})]})]})]});}
            var Q3;
            Q3=makeQuery(id+"F6.opExtrude","CAP_EDGE",EDGE,{"disambiguationData":[OSD([sQuery(id+"F0.wireOp",EDGE,"E7")])],"isStart":false});
            var Q4;
            Q4=makeQuery(id+"F6.opExtrude","CAP_EDGE",EDGE,{"disambiguationData":[OSD([sQuery(id+"F0.wireOp",EDGE,"E11")])],"isStart":false});
            var Q5;
            {var subQ0=sQuery(id+"F0.wireOp",EDGE,"E8");var subQ1=sQuery(id+"F0.wireOp",EDGE,"E3");var subQ2=sQuery(id+"F0.wireOp",EDGE,"E2");Q5=makeQuery(id+"F10.boolean.opBoolean","MERGE",EDGE,{"derivedFrom":[makeQuery(id+"F6.boolean.opBoolean","MERGE",EDGE,{"derivedFrom":[makeQuery(id+"F1.opExtrude","SWEPT_EDGE",EDGE,{"disambiguationData":[OSD([subQ2,subQ1,subQ0])]}),makeQuery(id+"F6.opExtrude","SWEPT_EDGE",EDGE,{"disambiguationData":[OSD([subQ2,subQ1,subQ0])]})]}),makeQuery(id+"F10.opExtrude","SWEPT_EDGE",EDGE,{"disambiguationData":[OSD([subQ2,subQ1,subQ0])]})]});}
            var Q6;
            Q6=makeQuery(id+"F10.opExtrude","CAP_EDGE",EDGE,{"disambiguationData":[OSD([sQuery(id+"F0.wireOp",EDGE,"E2")])],"isStart":false});
            var Q7;
            {var subQ0=sQuery(id+"F4.wireOp",EDGE,"E17");var subQ1=makeQuery(id+"F5.opExtrude","SWEPT_FACE",FACE,{"disambiguationData":[OSD([subQ0])]});var subQ2=makeQuery(id+"F3.opExtrude","SWEPT_FACE",FACE,{"disambiguationData":[OSD([sQuery(id+"F2.wireOp",EDGE,"E14")])]});var subQ3=sQuery(id+"F0.wireOp",EDGE,"E1");var subQ4=makeQuery(id+"F1.opExtrude","SWEPT_FACE",FACE,{"disambiguationData":[OSD([subQ3])]});var subQ5=sQuery(id+"F0.wireOp",EDGE,"E7");var subQ6=sQuery(id+"F0.wireOp",EDGE,"E5");var subQ7=sQuery(id+"F0.wireOp",EDGE,"E4");var subQ8=sQuery(id+"F0.wireOp",EDGE,"E2");var subQ9=makeQuery(id+"F1.opExtrude","CAP_FACE",FACE,{"disambiguationData":[OSD([sQuery(id+"F0.wireOp",EDGE,"E0"),subQ3,subQ8,subQ7,subQ6,subQ5,sQuery(id+"F0.wireOp",EDGE,"E8"),sQuery(id+"F0.wireOp",EDGE,"E9"),sQuery(id+"F0.wireOp",EDGE,"E10"),sQuery(id+"F0.wireOp",EDGE,"E11"),sQuery(id+"F0.wireOp",EDGE,"E12"),sQuery(id+"F0.wireOp",EDGE,"E13")])],"isStart":false});var subQ10=makeQuery(id+"F5.opExtrude","CAP_FACE",FACE,{"disambiguationData":[OSD([sQuery(id+"F4.wireOp",EDGE,"E16"),subQ0])],"isStart":true});var subQ11=makeQuery(id+"F5.opExtrude","CAP_EDGE",EDGE,{"disambiguationData":[OSD([subQ0])],"isStart":true});Q7=makeQuery(id+"F13.boolean.opBoolean","MERGE",EDGE,{"derivedFrom":[makeQuery(id+"F10.opExtrude","CAP_EDGE",EDGE,{"disambiguationData":[OSD([subQ0]),TDD([makeQuery(id+"F5.boolean.opBoolean","SPLIT",EDGE,{"disambiguationData":[TD([subQ9,subQ4,makeQuery(id+"F1.opExtrude","SWEPT_FACE",FACE,{"disambiguationData":[OSD([subQ8])]}),makeQuery(id+"F1.opExtrude","SWEPT_FACE",FACE,{"disambiguationData":[OSD([subQ7])]}),subQ2,subQ10,subQ1])],"derivedFrom":subQ11})])],"isStart":false}),makeQuery(id+"F10.opExtrude","CAP_EDGE",EDGE,{"disambiguationData":[OSD([subQ0]),TDD([makeQuery(id+"F5.boolean.opBoolean","SPLIT",EDGE,{"disambiguationData":[TD([subQ9,subQ4,makeQuery(id+"F1.opExtrude","SWEPT_FACE",FACE,{"disambiguationData":[OSD([subQ6])]}),makeQuery(id+"F1.opExtrude","SWEPT_FACE",FACE,{"disambiguationData":[OSD([subQ5])]}),subQ2,subQ10,subQ1])],"derivedFrom":subQ11})])],"isStart":false}),makeQuery(id+"F13.opExtrude","TWEAK_EDGE",EDGE,{"derivedFrom":[makeQuery(id+"F5.boolean.opBoolean","MERGE",FACE,{"derivedFrom":[makeQuery(id+"F3.boolean.opBoolean","MERGE",FACE,{"derivedFrom":[subQ4,subQ2]}),subQ1]}),makeQuery(id+"F12.opExtrude","TWEAK_EDGE",EDGE,{"derivedFrom":[makeQuery(id+"F11.imprint","IMPRINT",EDGE,{"derivedFrom":sQuery(id+"F11.wireOp",EDGE,"E19.top")}),makeQuery(id+"F11.imprint","IMPRINT",EDGE,{"derivedFrom":sQuery(id+"F11.wireOp",EDGE,"E19.left")})]})]})]});}
            var Q8;
            Q8=makeQuery(id+"F10.opExtrude","CAP_EDGE",EDGE,{"disambiguationData":[OSD([sQuery(id+"F0.wireOp",EDGE,"E8")])],"isStart":false});
            var Q9;
            Q9=makeQuery(id+"F10.opExtrude","CAP_EDGE",EDGE,{"disambiguationData":[OSD([sQuery(id+"F0.wireOp",EDGE,"E7")])],"isStart":false});
            var Q10;
            Q10=makeQuery(id+"F10.opExtrude","CAP_EDGE",EDGE,{"disambiguationData":[OSD([sQuery(id+"F0.wireOp",EDGE,"E11")])],"isStart":false});
            var Q11;
            {var subQ0=sQuery(id+"F0.wireOp",EDGE,"E11");var subQ1=sQuery(id+"F0.wireOp",EDGE,"E7");var subQ2=sQuery(id+"F0.wireOp",EDGE,"E6");Q11=makeQuery(id+"F10.boolean.opBoolean","MERGE",EDGE,{"derivedFrom":[makeQuery(id+"F6.boolean.opBoolean","MERGE",EDGE,{"derivedFrom":[makeQuery(id+"F1.opExtrude","SWEPT_EDGE",EDGE,{"disambiguationData":[OSD([subQ2,subQ1,subQ0])]}),makeQuery(id+"F6.opExtrude","SWEPT_EDGE",EDGE,{"disambiguationData":[OSD([subQ2,subQ1,subQ0])]})]}),makeQuery(id+"F10.opExtrude","SWEPT_EDGE",EDGE,{"disambiguationData":[OSD([subQ2,subQ1,subQ0])]})]});}
            fillet(context, id + "F16", {"entities" : qUnion([Q0, Q1, Q2, Q3, Q4, Q5, Q6, Q7, Q8, Q9, Q10, Q11]), "radius" : 5 * mm, "tangentPropagation" : true, "allowEdgeOverflow" : false});
        }
        {
            var Q0;
            {var subQ0=sQuery(id+"F0.wireOp",EDGE,"E12");var subQ1=sQuery(id+"F0.wireOp",EDGE,"E11");Q0=makeQuery(id+"F10.boolean.opBoolean","MERGE",EDGE,{"derivedFrom":[makeQuery(id+"F6.boolean.opBoolean","MERGE",EDGE,{"derivedFrom":[makeQuery(id+"F1.opExtrude","SWEPT_EDGE",EDGE,{"disambiguationData":[OSD([subQ1,subQ0])]}),makeQuery(id+"F6.opExtrude","SWEPT_EDGE",EDGE,{"disambiguationData":[OSD([subQ1,subQ0])]})]}),makeQuery(id+"F10.opExtrude","SWEPT_EDGE",EDGE,{"disambiguationData":[OSD([subQ1,subQ0])]})]});}
            fillet(context, id + "F17", {"entities" : qUnion([Q0]), "radius" : 2.5 * mm, "tangentPropagation" : true, "allowEdgeOverflow" : false});
        }
    });
